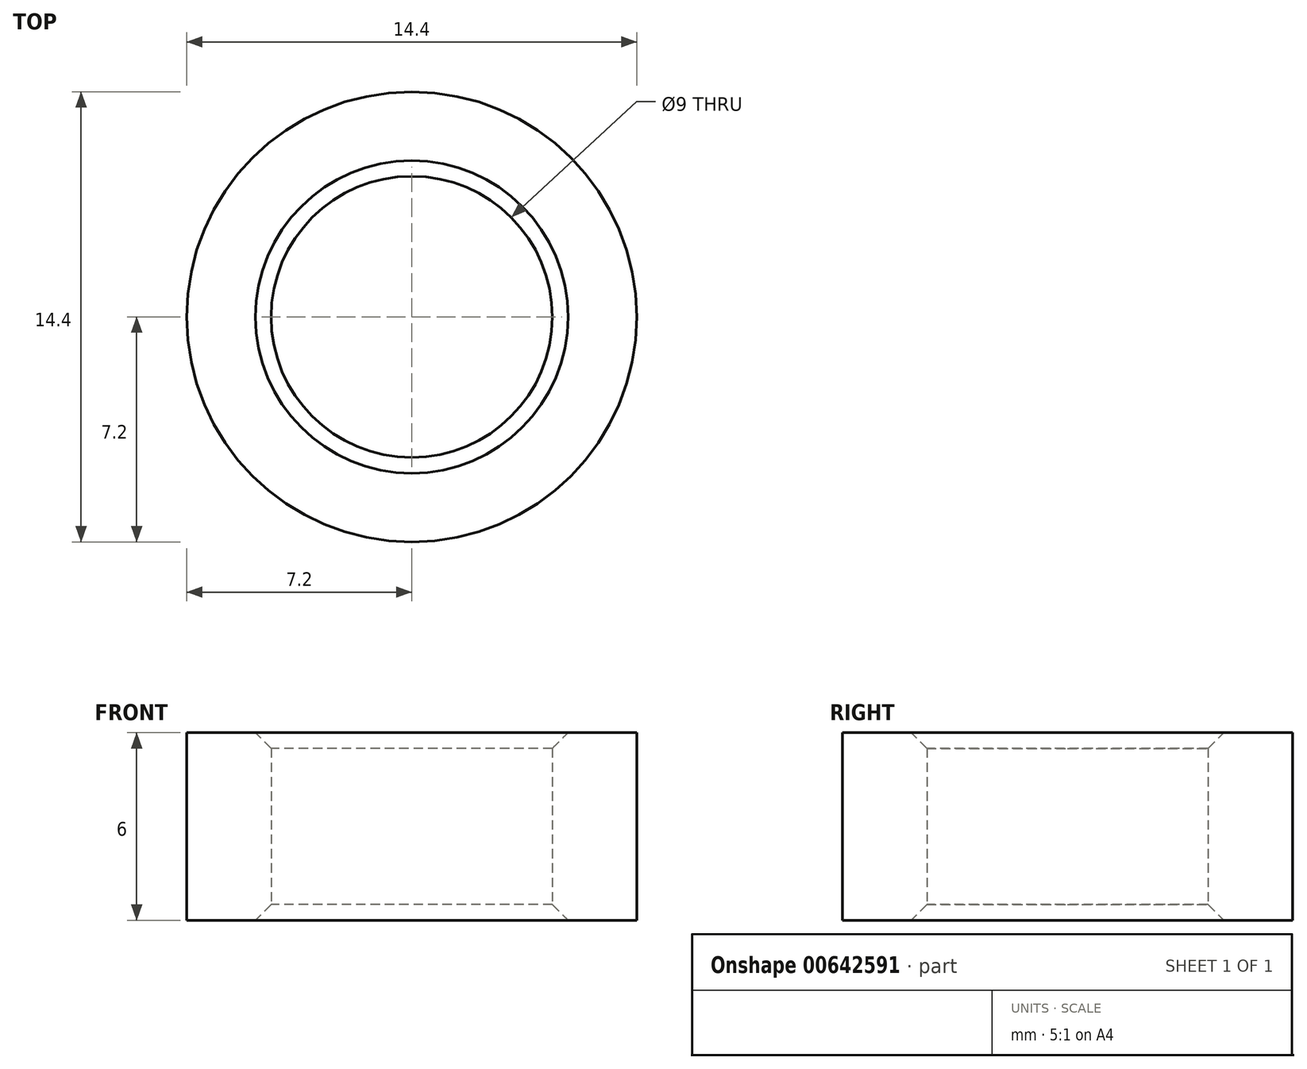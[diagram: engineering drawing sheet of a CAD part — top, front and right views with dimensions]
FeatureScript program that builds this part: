
annotation { "Feature Type Name" : "Feature", "Feature Type Description" : "" }
export const myFeature = defineFeature(function(context is Context, id is Id, definition is map)
    precondition{}
    {
        {
            var Q0;
            Q0=qCreatedBy(makeId("Top.planeOp"),FACE);
            var sketch = newSketch(context, id + "F0", { "sketchPlane" : qUnion([Q0])});
            skCircle(sketch, "E0", {"center": v(0, 0) * mm, "radius": 4.5 * mm});
            skCircle(sketch, "E1", {"center": v(0, 0) * mm, "radius": 7.2 * mm});
            skSolve(sketch);
        }
        {
            var Q0;
            Q0=makeQuery(id+"F0.imprint","IMPRINT",FACE,{"disambiguationData":[TD([[makeQuery(id+"F0.imprint","IMPRINT",EDGE,{"derivedFrom":sQuery(id+"F0.wireOp",EDGE,"E0")}),-1.0]])]});
            extrude(context, id + "F1", {"entities" : qUnion([Q0]), "depth" : 6 * mm, "offsetDistance" : 25 * mm});
        }
        {
            var Q0;
            Q0=makeQuery(id+"F1.opExtrude","CAP_EDGE",EDGE,{"disambiguationData":[OSD([sQuery(id+"F0.wireOp",EDGE,"E0")])],"isStart":false});
            chamfer(context, id + "F2", {"entities" : qUnion([Q0]), "chamferType" : ChamferType.OFFSET_ANGLE, "width" : 0.5 * mm, "oppositeDirection" : false, "angle" : 45 * degree, "tangentPropagation" : true});
        }
        {
            var Q0;
            Q0=makeQuery(id+"F1.opExtrude","CAP_EDGE",EDGE,{"disambiguationData":[OSD([sQuery(id+"F0.wireOp",EDGE,"E0")])],"isStart":true});
            chamfer(context, id + "F3", {"entities" : qUnion([Q0]), "chamferType" : ChamferType.OFFSET_ANGLE, "width" : .5 * mm, "oppositeDirection" : false, "angle" : 45 * degree, "tangentPropagation" : true});
        }
    });
